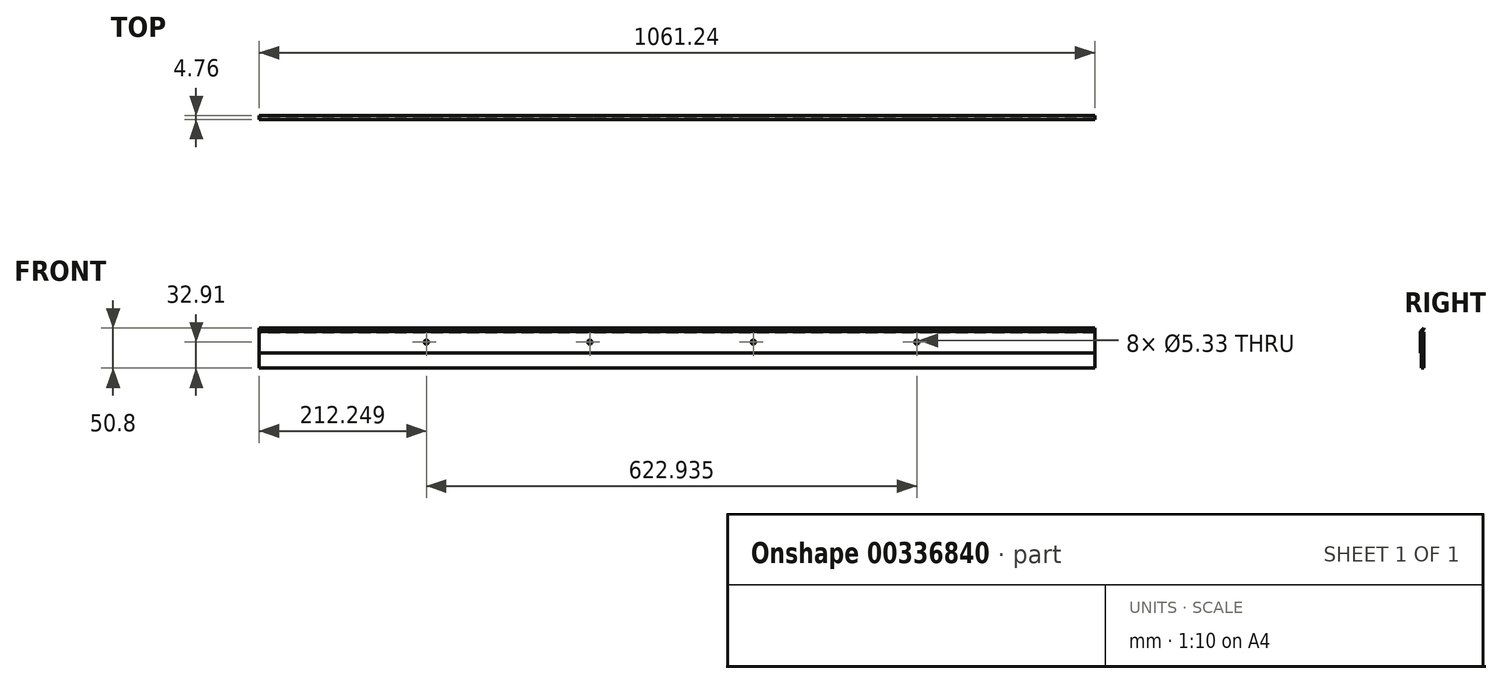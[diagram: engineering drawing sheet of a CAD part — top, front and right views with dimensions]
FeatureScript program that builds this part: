
annotation { "Feature Type Name" : "Feature", "Feature Type Description" : "" }
export const myFeature = defineFeature(function(context is Context, id is Id, definition is map)
    precondition{}
    {
        {
            var Q0;
            Q0=qCreatedBy(makeId("Right.planeOp"),FACE);
            var sketch = newSketch(context, id + "F0", { "sketchPlane" : qUnion([Q0])});
            skLineSegment(sketch, "E0", {"start": v(0, 0) * mm, "end": v(0, -2.07) * mm});
            skLineSegment(sketch, "E1", {"start": v(0, -2.07) * mm, "end": v(-3.17, -4.75) * mm});
            skLineSegment(sketch, "E2", {"start": v(-3.17, -4.75) * mm, "end": v(0, -4.75) * mm});
            skLineSegment(sketch, "E3", {"start": v(0, -4.75) * mm, "end": v(0, -6.34) * mm});
            skLineSegment(sketch, "E4", {"start": v(0, -6.34) * mm, "end": v(-3.17, -6.34) * mm});
            skLineSegment(sketch, "E5", {"start": v(-3.17, -6.34) * mm, "end": v(-3.17, -31.75) * mm});
            skLineSegment(sketch, "E6", {"start": v(-3.17, -31.75) * mm, "end": v(-4.76, -31.75) * mm});
            skLineSegment(sketch, "E7", {"start": v(-4.76, -31.75) * mm, "end": v(-4.76, -4.03) * mm});
            skLineSegment(sketch, "E8", {"start": v(-4.76, -4.03) * mm, "end": v(0, 0) * mm});
            skLineSegment(sketch, "E9", {"start": v(-0.93, -2.85) * mm, "end": v(-1.78, -1.5) * mm, "construction": true});
            skSolve(sketch);
        }
        {
            var Q0;
            Q0=makeQuery(id+"F0.imprint","IMPRINT",FACE,{"disambiguationData":[TD([[makeQuery(id+"F0.imprint","IMPRINT",EDGE,{"derivedFrom":sQuery(id+"F0.wireOp",EDGE,"E0")}),-1.0]])]});
            extrude(context, id + "F1", {"entities" : qUnion([Q0]), "depth" : 1061.24 * mm});
        }
        {
            var Q0;
            Q0=qCreatedBy(makeId("Right.planeOp"),FACE);
            var sketch = newSketch(context, id + "F2", { "sketchPlane" : qUnion([Q0])});
            skPoint(sketch, "E10.0", {"position": v(-3.17, -6.34) * mm});
            skLineSegment(sketch, "E11.bottom", {"start": v(0, -6.34) * mm, "end": v(-3.17, -6.34) * mm});
            skLineSegment(sketch, "E11.top", {"start": v(0, -50.8) * mm, "end": v(-3.17, -50.8) * mm});
            skLineSegment(sketch, "E11.left", {"start": v(0, -6.34) * mm, "end": v(0, -50.8) * mm});
            skLineSegment(sketch, "E11.right", {"start": v(-3.17, -6.34) * mm, "end": v(-3.17, -50.8) * mm});
            skSolve(sketch);
        }
        {
            var Q0;
            Q0 = qSketchRegion(id + "F2", true);
            var Q1;
            Q1=makeQuery(id+"F1.opExtrude","CAP_FACE",FACE,{"disambiguationData":[OSD([sQuery(id+"F0.wireOp",EDGE,"E0"),sQuery(id+"F0.wireOp",EDGE,"E1"),sQuery(id+"F0.wireOp",EDGE,"E2"),sQuery(id+"F0.wireOp",EDGE,"E3"),sQuery(id+"F0.wireOp",EDGE,"E4"),sQuery(id+"F0.wireOp",EDGE,"E5"),sQuery(id+"F0.wireOp",EDGE,"E6"),sQuery(id+"F0.wireOp",EDGE,"E7"),sQuery(id+"F0.wireOp",EDGE,"E8")])],"isStart":false});
            extrude(context, id + "F3", {"entities" : qUnion([Q0]), "endBound" : BoundingType.UP_TO_SURFACE, "endBoundEntityFace" : qUnion([Q1]), "depth" : 995.68 * mm});
        }
        {
            var Q0;
            Q0=makeQuery(id+"F1.opExtrude","SWEPT_FACE",FACE,{"disambiguationData":[OSD([sQuery(id+"F0.wireOp",EDGE,"E7")])]});
            var sketch = newSketch(context, id + "F4", { "sketchPlane" : qUnion([Q0])});
            skLineSegment(sketch, "E12", {"start": v(0, -31.75) * mm, "end": v(212.25, -31.75) * mm, "construction": true});
            skLineSegment(sketch, "E13", {"start": v(212.25, -31.75) * mm, "end": v(424.5, -31.75) * mm, "construction": true});
            skLineSegment(sketch, "E14", {"start": v(424.5, -31.75) * mm, "end": v(636.75, -31.75) * mm, "construction": true});
            skLineSegment(sketch, "E15", {"start": v(636.75, -31.75) * mm, "end": v(849, -31.75) * mm, "construction": true});
            skLineSegment(sketch, "E16", {"start": v(849, -31.75) * mm, "end": v(1061.24, -31.75) * mm, "construction": true});
            skCircle(sketch, "E17", {"center": v(212.25, -17.89) * mm, "radius": 2.67 * mm});
            skCircle(sketch, "E18.1.0.0", {"center": v(419.9, -17.89) * mm, "radius": 2.67 * mm});
            skCircle(sketch, "E18.2.0.0", {"center": v(627.54, -17.89) * mm, "radius": 2.67 * mm});
            skCircle(sketch, "E18.3.0.0", {"center": v(835.18, -17.89) * mm, "radius": 2.67 * mm});
            skLineSegment(sketch, "E18.direction1", {"start": v(212.25, -17.89) * mm, "end": v(419.9, -17.89) * mm, "construction": true});
            skSolve(sketch);
        }
        {
            var Q0;
            Q0 = qSketchRegion(id + "F4", true);
            extrude(context, id + "F5", {"entities" : qUnion([Q0]), "operationType" : NewBodyOperationType.REMOVE, "endBound" : BoundingType.THROUGH_ALL, "oppositeDirection" : true, "depth" : 25.4 * mm});
        }
    });
